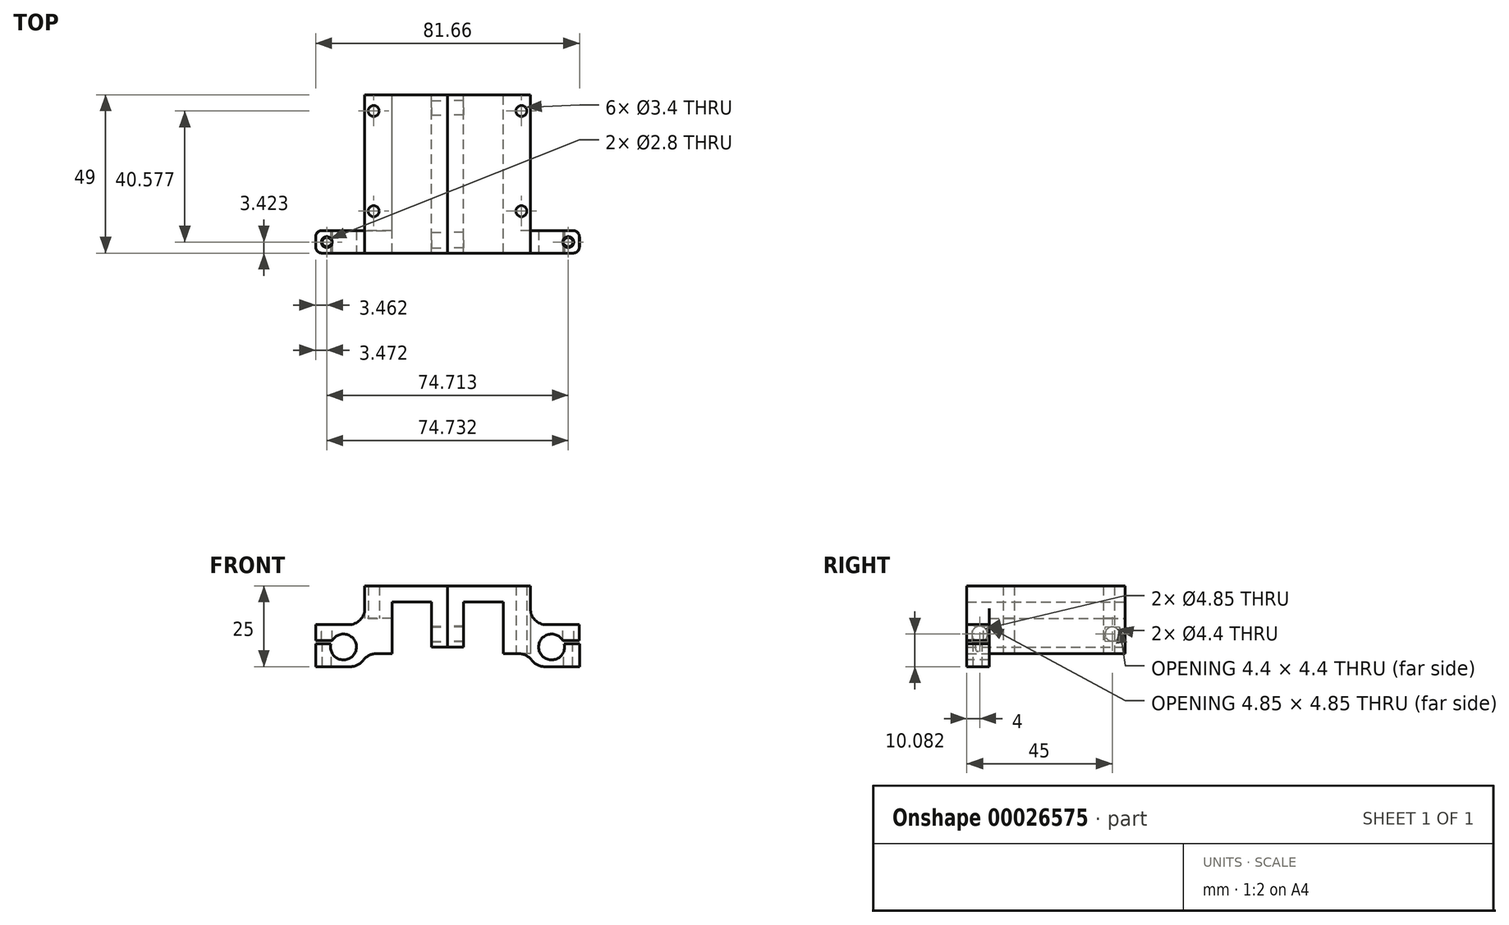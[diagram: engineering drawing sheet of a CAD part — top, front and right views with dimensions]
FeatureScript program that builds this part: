
annotation { "Feature Type Name" : "Feature", "Feature Type Description" : "" }
export const myFeature = defineFeature(function(context is Context, id is Id, definition is map)
    precondition{}
    {
        {
            var Q0;
            Q0=qCreatedBy(makeId("Front.planeOp"),FACE);
            var sketch = newSketch(context, id + "F0", { "sketchPlane" : qUnion([Q0])});
            skLineSegment(sketch, "E0", {"start": v(-20.67, 10.9) * mm, "end": v(-20.67, 29.8) * mm});
            skLineSegment(sketch, "E1", {"start": v(-20.67, 29.8) * mm, "end": v(4.94, 29.8) * mm});
            skLineSegment(sketch, "E2", {"start": v(4.94, 29.8) * mm, "end": v(4.94, 17.8) * mm});
            skLineSegment(sketch, "E3", {"start": v(-3.47, 8.8) * mm, "end": v(-3.47, 24.8) * mm});
            skLineSegment(sketch, "E4", {"start": v(-3.47, 24.8) * mm, "end": v(-15.67, 24.8) * mm});
            skLineSegment(sketch, "E5", {"start": v(-15.67, 24.8) * mm, "end": v(-15.67, 10.9) * mm});
            skLineSegment(sketch, "E6", {"start": v(-15.67, 10.9) * mm, "end": v(-20.67, 10.9) * mm});
            skLineSegment(sketch, "E7", {"start": v(4.94, 17.8) * mm, "end": v(4.94, 8.8) * mm});
            skLineSegment(sketch, "E8", {"start": v(4.94, 8.8) * mm, "end": v(-3.47, 8.8) * mm});
            skLineSegment(sketch, "E9", {"start": v(4.94, 17.8) * mm, "end": v(4.94, 17.8) * mm});
            skLineSegment(sketch, "E10", {"start": v(20.13, 17.79) * mm, "end": v(20.13, 12.88) * mm});
            skLineSegment(sketch, "E11", {"start": v(20.13, 12.88) * mm, "end": v(13.49, 12.88) * mm});
            skLineSegment(sketch, "E12", {"start": v(13.49, 12.88) * mm, "end": v(13.49, 11.89) * mm});
            skLineSegment(sketch, "E13", {"start": v(13.49, 11.89) * mm, "end": v(20.16, 11.89) * mm});
            skLineSegment(sketch, "E14", {"start": v(20.16, 11.89) * mm, "end": v(20.16, 4.8) * mm});
            skLineSegment(sketch, "E15", {"start": v(20.16, 4.8) * mm, "end": v(6.35, 4.8) * mm});
            skLineSegment(sketch, "E16", {"start": v(6.35, 4.8) * mm, "end": v(4.94, 8.8) * mm});
            skLineSegment(sketch, "E17", {"start": v(20.13, 17.79) * mm, "end": v(4.94, 17.8) * mm});
            skSolve(sketch);
        }
        {
            var Q0;
            Q0=makeQuery(id+"F0.imprint","IMPRINT",FACE,{"disambiguationData":[TD([[makeQuery(id+"F0.imprint","IMPRINT",EDGE,{"derivedFrom":sQuery(id+"F0.wireOp",EDGE,"E0")}),-1.0]])]});
            var Q1;
            {var subQ2=sQuery(id+"F0.wireOp",EDGE,"69cbcc5d-e0c3-48db-8baf-3487a8abab7d");Q1=makeQuery(id+"F0.imprint","IMPRINT",FACE,{"disambiguationData":[TD([[makeQuery(id+"F0.imprint","IMPRINT",EDGE,{"derivedFrom":subQ2}),-1.0]])]});}
            var Q2;
            Q2=makeQuery(id+"F0.imprint","IMPRINT",FACE,{"disambiguationData":[TD([[makeQuery(id+"F0.imprint","IMPRINT",EDGE,{"derivedFrom":sQuery(id+"F0.wireOp",EDGE,"E7")}),1.0]])]});
            extrude(context, id + "F1", {"entities" : qUnion([Q0, Q1, Q2]), "depth" : 7 * mm});
        }
        {
            var Q0;
            Q0=makeQuery(id+"F0.imprint","IMPRINT",FACE,{"disambiguationData":[TD([[makeQuery(id+"F0.imprint","IMPRINT",EDGE,{"derivedFrom":sQuery(id+"F0.wireOp",EDGE,"E0")}),-1.0]])]});
            extrude(context, id + "F2", {"entities" : qUnion([Q0]), "operationType" : NewBodyOperationType.ADD, "oppositeDirection" : true, "depth" : 42 * mm});
        }
        {
            var Q0;
            {var subQ0=sQuery(id+"F0.wireOp",EDGE,"E8");Q0=makeQuery(id+"F2.boolean.opBoolean","MERGE",FACE,{"derivedFrom":[makeQuery(id+"F1.opExtrude","SWEPT_FACE",FACE,{"disambiguationData":[OSD([subQ0])]}),makeQuery(id+"F2.opExtrude","SWEPT_FACE",FACE,{"disambiguationData":[OSD([subQ0])]})]});}
            var sketch = newSketch(context, id + "F3", { "sketchPlane" : qUnion([Q0])});
            skCircle(sketch, "E18", {"center": v(2.19, -6) * mm, "radius": 1.7 * mm});
            skCircle(sketch, "E19", {"center": v(2.19, -37) * mm, "radius": 1.7 * mm});
            skCircle(sketch, "E20", {"center": v(17.69, -21.5) * mm, "radius": 11 * mm});
            skSolve(sketch);
        }
        {
            var Q0;
            Q0=qSketchRegion(id+"F3",true);
            extrude(context, id + "F4", {"entities" : qUnion([Q0]), "operationType" : NewBodyOperationType.REMOVE, "endBound" : BoundingType.THROUGH_ALL, "oppositeDirection" : true, "depth" : 25 * mm});
        }
        {
            var Q0;
            Q0=makeQuery(id+"F1.opExtrude","CAP_FACE",FACE,{"disambiguationData":[OSD([sQuery(id+"F0.wireOp",EDGE,"E0"),sQuery(id+"F0.wireOp",EDGE,"E1"),sQuery(id+"F0.wireOp",EDGE,"E2"),sQuery(id+"F0.wireOp",EDGE,"E3"),sQuery(id+"F0.wireOp",EDGE,"E4"),sQuery(id+"F0.wireOp",EDGE,"E5"),sQuery(id+"F0.wireOp",EDGE,"E6"),sQuery(id+"F0.wireOp",EDGE,"E8"),sQuery(id+"F0.wireOp",EDGE,"E9"),sQuery(id+"F0.wireOp",EDGE,"58f11638-63e7-4b32-8aff-a1ba3c53649b"),sQuery(id+"F0.wireOp",EDGE,"E10"),sQuery(id+"F0.wireOp",EDGE,"E11"),sQuery(id+"F0.wireOp",EDGE,"E12"),sQuery(id+"F0.wireOp",EDGE,"E13"),sQuery(id+"F0.wireOp",EDGE,"E14"),sQuery(id+"F0.wireOp",EDGE,"E15"),sQuery(id+"F0.wireOp",EDGE,"E16")])],"isStart":false});
            var sketch = newSketch(context, id + "F5", { "sketchPlane" : qUnion([Q0])});
            skCircle(sketch, "E21", {"center": v(11.53, 10.9) * mm, "radius": 4 * mm});
            skSolve(sketch);
        }
        {
            var Q0;
            Q0=qSketchRegion(id+"F5",true);
            extrude(context, id + "F6", {"entities" : qUnion([Q0]), "operationType" : NewBodyOperationType.REMOVE, "oppositeDirection" : true, "depth" : 10 * mm});
        }
        {
            var Q0;
            Q0=qSketchRegion(id+"F3",true);
            extrude(context, id + "F7", {"entities" : qUnion([Q0]), "operationType" : NewBodyOperationType.REMOVE, "endBound" : BoundingType.THROUGH_ALL, "oppositeDirection" : true, "depth" : 25 * mm});
        }
        {
            var Q0;
            Q0=makeQuery(id+"F1.opExtrude","SWEPT_FACE",FACE,{"disambiguationData":[OSD([sQuery(id+"F0.wireOp",EDGE,"E17")])]});
            var sketch = newSketch(context, id + "F8", { "sketchPlane" : qUnion([Q0])});
            skCircle(sketch, "E22", {"center": v(16.67, -3.58) * mm, "radius": 1.7 * mm});
            skCircle(sketch, "E23", {"center": v(16.67, -3.58) * mm, "radius": 1.4 * mm});
            skSolve(sketch);
        }
        {
            var Q0;
            Q0=makeQuery(id+"F8.imprint","IMPRINT",FACE,{"disambiguationData":[TD([[makeQuery(id+"F8.imprint","IMPRINT",EDGE,{"derivedFrom":sQuery(id+"F8.wireOp",EDGE,"E23")}),1.0]])]});
            extrude(context, id + "F9", {"entities" : qUnion([Q0]), "operationType" : NewBodyOperationType.REMOVE, "endBound" : BoundingType.THROUGH_ALL, "oppositeDirection" : true, "depth" : 25 * mm});
        }
        {
            var Q0;
            Q0=makeQuery(id+"F8.imprint","IMPRINT",FACE,{"disambiguationData":[TD([[makeQuery(id+"F8.imprint","IMPRINT",EDGE,{"derivedFrom":sQuery(id+"F8.wireOp",EDGE,"E22")}),1.0]])]});
            extrude(context, id + "F10", {"entities" : qUnion([Q0]), "operationType" : NewBodyOperationType.REMOVE, "endBound" : BoundingType.UP_TO_NEXT, "oppositeDirection" : true, "depth" : 25 * mm});
        }
        {
            var Q0;
            Q0=makeQuery(id+"F1.opExtrude","SWEPT_EDGE",EDGE,{"disambiguationData":[OSD([sQuery(id+"F0.wireOp",EDGE,"E2"),sQuery(id+"F0.wireOp",EDGE,"E7"),sQuery(id+"F0.wireOp",EDGE,"E17")])]});
            fillet(context, id + "F11", {"entities" : qUnion([Q0]), "radius" : 5 * mm, "tangentPropagation" : true, "allowEdgeOverflow" : false});
        }
        {
            var Q0;
            Q0=makeQuery(id+"F1.opExtrude","SWEPT_EDGE",EDGE,{"disambiguationData":[OSD([sQuery(id+"F0.wireOp",EDGE,"E7"),sQuery(id+"F0.wireOp",EDGE,"E8"),sQuery(id+"F0.wireOp",EDGE,"E16")])]});
            fillet(context, id + "F12", {"entities" : qUnion([Q0]), "radius" : 5 * mm, "tangentPropagation" : true, "allowEdgeOverflow" : false});
        }
        {
            var Q0;
            Q0=makeQuery(id+"F1.opExtrude","SWEPT_EDGE",EDGE,{"disambiguationData":[OSD([sQuery(id+"F0.wireOp",EDGE,"E15"),sQuery(id+"F0.wireOp",EDGE,"E16")])]});
            fillet(context, id + "F13", {"entities" : qUnion([Q0]), "radius" : 5 * mm, "tangentPropagation" : true, "allowEdgeOverflow" : false});
        }
        {
            var Q0;
            Q0=makeQuery(id+"F1.opExtrude","CAP_EDGE",EDGE,{"disambiguationData":[OSD([sQuery(id+"F0.wireOp",EDGE,"E10")])],"isStart":false});
            var Q1;
            Q1=makeQuery(id+"F1.opExtrude","CAP_EDGE",EDGE,{"disambiguationData":[OSD([sQuery(id+"F0.wireOp",EDGE,"E14")])],"isStart":false});
            var Q2;
            Q2=makeQuery(id+"F1.opExtrude","CAP_EDGE",EDGE,{"disambiguationData":[OSD([sQuery(id+"F0.wireOp",EDGE,"E10")])],"isStart":true});
            var Q3;
            Q3=makeQuery(id+"F1.opExtrude","CAP_EDGE",EDGE,{"disambiguationData":[OSD([sQuery(id+"F0.wireOp",EDGE,"E14")])],"isStart":true});
            fillet(context, id + "F14", {"entities" : qUnion([Q0, Q1, Q2, Q3]), "radius" : 2 * mm, "tangentPropagation" : true, "allowEdgeOverflow" : false});
        }
        {
            var Q0;
            {var subQ0=sQuery(id+"F0.wireOp",EDGE,"E0");Q0=makeQuery(id+"F2.boolean.opBoolean","MERGE",FACE,{"derivedFrom":[makeQuery(id+"F1.opExtrude","SWEPT_FACE",FACE,{"disambiguationData":[OSD([subQ0])]}),makeQuery(id+"F2.opExtrude","SWEPT_FACE",FACE,{"disambiguationData":[OSD([subQ0])]})]});}
            var sketch = newSketch(context, id + "F15", { "sketchPlane" : qUnion([Q0])});
            skCircle(sketch, "E24", {"center": v(-38, 14.9) * mm, "radius": 2.2 * mm});
            skCircle(sketch, "E25", {"center": v(3, 14.9) * mm, "radius": 2.43 * mm});
            skSolve(sketch);
        }
        {
            var Q0;
            Q0=qSketchRegion(id+"F15",true);
            extrude(context, id + "F16", {"entities" : qUnion([Q0]), "operationType" : NewBodyOperationType.REMOVE, "oppositeDirection" : true, "depth" : 6 * mm});
        }
        {
            var Q0;
            Q0=makeQuery(id+"F1.opExtrude","SWEPT_BODY",BODY,{"disambiguationData":[OSD([sQuery(id+"F0.wireOp",EDGE,"E0"),sQuery(id+"F0.wireOp",EDGE,"E1"),sQuery(id+"F0.wireOp",EDGE,"E2"),sQuery(id+"F0.wireOp",EDGE,"E3"),sQuery(id+"F0.wireOp",EDGE,"E4"),sQuery(id+"F0.wireOp",EDGE,"E5"),sQuery(id+"F0.wireOp",EDGE,"E6"),sQuery(id+"F0.wireOp",EDGE,"E8"),sQuery(id+"F0.wireOp",EDGE,"E10"),sQuery(id+"F0.wireOp",EDGE,"E11"),sQuery(id+"F0.wireOp",EDGE,"E12"),sQuery(id+"F0.wireOp",EDGE,"E13"),sQuery(id+"F0.wireOp",EDGE,"E14"),sQuery(id+"F0.wireOp",EDGE,"E15"),sQuery(id+"F0.wireOp",EDGE,"E16"),sQuery(id+"F0.wireOp",EDGE,"E17")])]});
            var Q1;
            {var subQ0=sQuery(id+"F0.wireOp",EDGE,"E0");Q1=makeQuery(id+"F2.boolean.opBoolean","MERGE",FACE,{"derivedFrom":[makeQuery(id+"F1.opExtrude","SWEPT_FACE",FACE,{"disambiguationData":[OSD([subQ0])]}),makeQuery(id+"F2.opExtrude","SWEPT_FACE",FACE,{"disambiguationData":[OSD([subQ0])]})]});}
            mirror(context, id + "F17", {"entities" : qUnion([Q0]), "mirrorPlane" : qUnion([Q1])});
        }
        {
            var Q0;
            Q0=makeQuery(id+"F17.opPattern","COPY",FACE,{"derivedFrom":makeQuery(id+"F2.opExtrude","CAP_FACE",FACE,{"disambiguationData":[OSD([sQuery(id+"F0.wireOp",EDGE,"E0"),sQuery(id+"F0.wireOp",EDGE,"E1"),sQuery(id+"F0.wireOp",EDGE,"E2"),sQuery(id+"F0.wireOp",EDGE,"E3"),sQuery(id+"F0.wireOp",EDGE,"E4"),sQuery(id+"F0.wireOp",EDGE,"E5"),sQuery(id+"F0.wireOp",EDGE,"E6"),sQuery(id+"F0.wireOp",EDGE,"E7"),sQuery(id+"F0.wireOp",EDGE,"E8")])],"isStart":false}),"instanceName":"1"});
            var sketch = newSketch(context, id + "F18", { "sketchPlane" : qUnion([Q0])});
            skLineSegment(sketch, "E26.bottom", {"start": v(37.87, 8.8) * mm, "end": v(46.28, 8.8) * mm});
            skLineSegment(sketch, "E26.top", {"start": v(37.87, 19.74) * mm, "end": v(46.28, 19.74) * mm});
            skLineSegment(sketch, "E26.left", {"start": v(37.87, 8.8) * mm, "end": v(37.87, 19.74) * mm});
            skLineSegment(sketch, "E26.right", {"start": v(46.28, 8.8) * mm, "end": v(46.28, 19.74) * mm});
            skSolve(sketch);
        }
        {
            var Q0;
            Q0=qSketchRegion(id+"F18",true);
            var Q1;
            Q1=makeQuery(id+"F17.opPattern","COPY",FACE,{"derivedFrom":makeQuery(id+"F1.opExtrude","CAP_FACE",FACE,{"disambiguationData":[OSD([sQuery(id+"F0.wireOp",EDGE,"E0"),sQuery(id+"F0.wireOp",EDGE,"E1"),sQuery(id+"F0.wireOp",EDGE,"E2"),sQuery(id+"F0.wireOp",EDGE,"E3"),sQuery(id+"F0.wireOp",EDGE,"E4"),sQuery(id+"F0.wireOp",EDGE,"E5"),sQuery(id+"F0.wireOp",EDGE,"E6"),sQuery(id+"F0.wireOp",EDGE,"E8"),sQuery(id+"F0.wireOp",EDGE,"E10"),sQuery(id+"F0.wireOp",EDGE,"E11"),sQuery(id+"F0.wireOp",EDGE,"E12"),sQuery(id+"F0.wireOp",EDGE,"E13"),sQuery(id+"F0.wireOp",EDGE,"E14"),sQuery(id+"F0.wireOp",EDGE,"E15"),sQuery(id+"F0.wireOp",EDGE,"E16"),sQuery(id+"F0.wireOp",EDGE,"E17")])],"isStart":true}),"instanceName":"1"});
            extrude(context, id + "F19", {"entities" : qUnion([Q0]), "operationType" : NewBodyOperationType.REMOVE, "endBound" : BoundingType.UP_TO_SURFACE, "oppositeDirection" : true, "endBoundEntityFace" : qUnion([Q1]), "depth" : 25 * mm});
        }
    });
